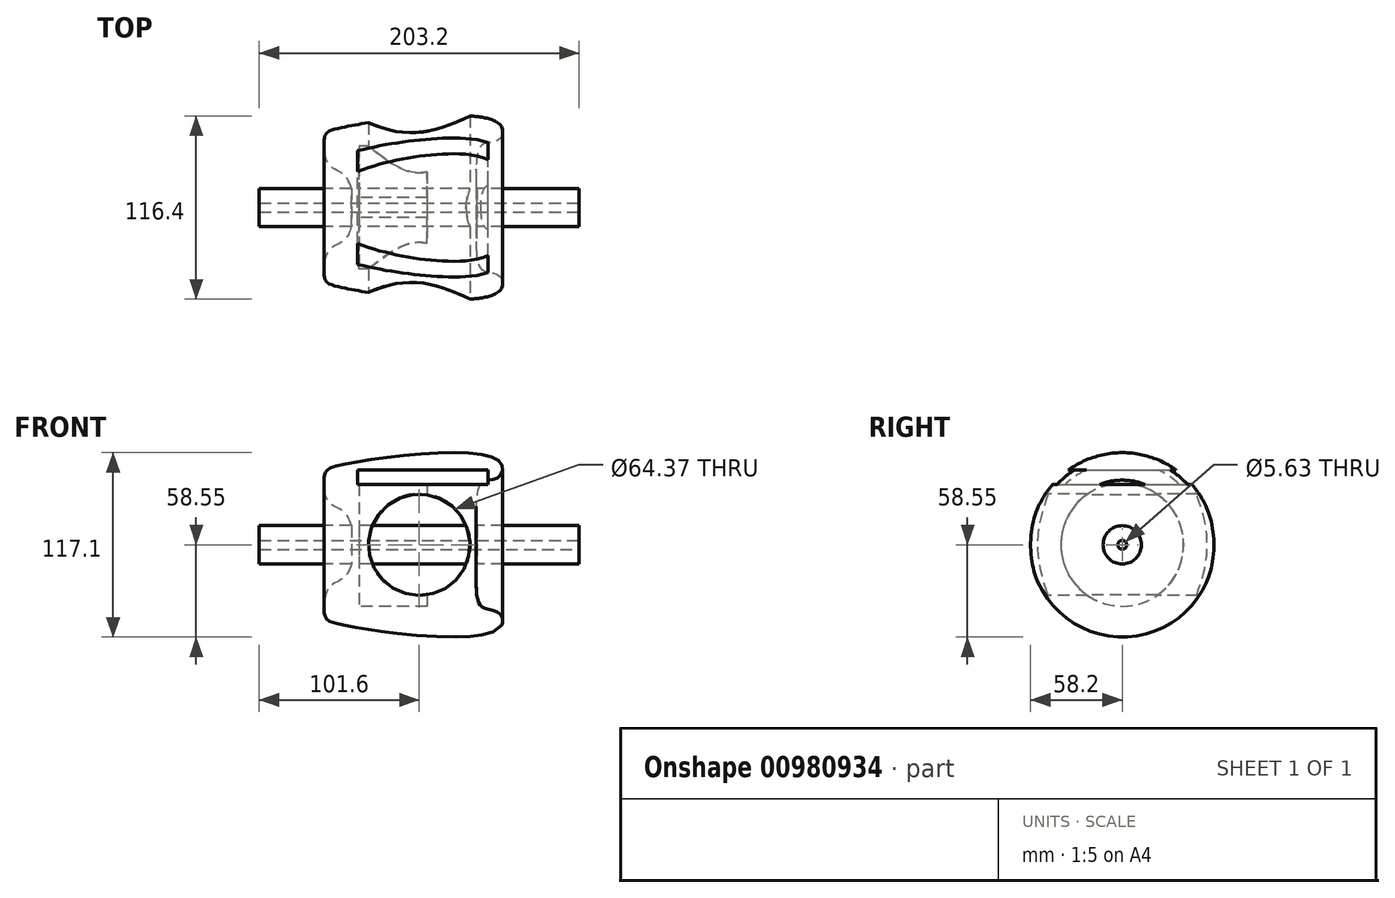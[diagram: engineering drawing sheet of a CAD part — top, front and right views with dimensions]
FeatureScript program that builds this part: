
annotation { "Feature Type Name" : "Feature", "Feature Type Description" : "" }
export const myFeature = defineFeature(function(context is Context, id is Id, definition is map)
    precondition{}
    {
        {
            var Q0;
            Q0=qCreatedBy(makeId("Front.planeOp"),FACE);
            var sketch = newSketch(context, id + "F0", { "sketchPlane" : qUnion([Q0])});
            skFitSpline(sketch, "E0", {"points": [v(-40.54, 0) * mm, v(-47.36, 20.34) * mm, v(-57.74, 27.7) * mm, v(-60.2, 44.09) * mm, v(-52.28, 50.1) * mm, v(49.82, 53.92) * mm, v(50.37, 43) * mm, v(39.45, 39.17) * mm, v(36.44, 15.42) * mm, v(37, 0) * mm], "startDerivative": vector(-37.15, 216.85) * mm, "endDerivative": vector(3.87, -138.09) * mm});
            skLineSegment(sketch, "E1", {"start": v(-86.95, 0) * mm, "end": v(97.05, 0) * mm, "construction": true});
            skLineSegment(sketch, "E2", {"start": v(-40.54, 0) * mm, "end": v(-38.13, 0) * mm});
            skLineSegment(sketch, "E3", {"start": v(-38.13, 0) * mm, "end": v(-38.13, 39) * mm});
            skLineSegment(sketch, "E4", {"start": v(-38.13, 39) * mm, "end": v(4.98, 39) * mm});
            skLineSegment(sketch, "E5", {"start": v(4.98, 39) * mm, "end": v(4.98, 0) * mm});
            skLineSegment(sketch, "E6", {"start": v(4.98, 0) * mm, "end": v(37, 0) * mm});
            skSolve(sketch);
        }
        {
            var Q0;
            Q0 = qSketchRegion(id + "F0", true);
            var Q1;
            Q1=sQuery(id+"F0.wireOp",EDGE,"E1");
            revolve(context, id + "F1", {"surfaceOperationType" : NewSurfaceOperationType.NEW, "entities" : qUnion([Q0]), "axis" : qUnion([Q1]), "revolveType" : RevolveType.FULL});
        }
        {
            var Q0;
            Q0=qCreatedBy(makeId("Front.planeOp"),FACE);
            var sketch = newSketch(context, id + "F2", { "sketchPlane" : qUnion([Q0])});
            skCircle(sketch, "E7", {"center": v(0, 0) * mm, "radius": 32.18 * mm});
            skSolve(sketch);
        }
        {
            var Q0;
            Q0 = qSketchRegion(id + "F2", true);
            extrude(context, id + "F3", {"entities" : qUnion([Q0]), "operationType" : NewBodyOperationType.REMOVE, "endBound" : BoundingType.SYMMETRIC, "oppositeDirection" : true, "depth" : 127 * mm, "offsetDistance" : 25.4 * mm});
        }
        {
            var Q0;
            Q0=qCreatedBy(makeId("Right.planeOp"),FACE);
            var sketch = newSketch(context, id + "F4", { "sketchPlane" : qUnion([Q0])});
            skCircle(sketch, "E8", {"center": v(0, 0) * mm, "radius": 12.2 * mm});
            skSolve(sketch);
        }
        {
            var Q0;
            Q0 = qSketchRegion(id + "F4", true);
            extrude(context, id + "F5", {"entities" : qUnion([Q0]), "operationType" : NewBodyOperationType.ADD, "endBound" : BoundingType.SYMMETRIC, "depth" : 203.2 * mm, "offsetDistance" : 25.4 * mm});
        }
        {
            var Q0;
            Q0=makeQuery(id+"F5.opExtrude","CAP_FACE",FACE,{"disambiguationData":[OSD([sQuery(id+"F4.wireOp",EDGE,"E8")])],"isStart":false});
            var sketch = newSketch(context, id + "F6", { "sketchPlane" : qUnion([Q0])});
            skCircle(sketch, "E9", {"center": v(0, 0) * mm, "radius": 2.81 * mm});
            skSolve(sketch);
        }
        {
            var Q0;
            Q0 = qSketchRegion(id + "F6", true);
            extrude(context, id + "F7", {"entities" : qUnion([Q0]), "operationType" : NewBodyOperationType.REMOVE, "endBound" : BoundingType.THROUGH_ALL, "oppositeDirection" : true, "depth" : 25.4 * mm, "offsetDistance" : 25.4 * mm});
        }
        {
            var Q0;
            Q0=qCreatedBy(makeId("Front.planeOp"),FACE);
            var sketch = newSketch(context, id + "F8", { "sketchPlane" : qUnion([Q0])});
            skLineSegment(sketch, "E10.bottom", {"start": v(-39.13, 47.54) * mm, "end": v(43.8, 47.54) * mm});
            skLineSegment(sketch, "E10.top", {"start": v(-39.13, 38.5) * mm, "end": v(43.8, 38.5) * mm});
            skLineSegment(sketch, "E10.left", {"start": v(-39.13, 47.54) * mm, "end": v(-39.13, 38.5) * mm});
            skLineSegment(sketch, "E10.right", {"start": v(43.8, 47.54) * mm, "end": v(43.8, 38.5) * mm});
            skSolve(sketch);
        }
        {
            var Q0;
            Q0 = qSketchRegion(id + "F8", true);
            extrude(context, id + "F9", {"entities" : qUnion([Q0]), "operationType" : NewBodyOperationType.REMOVE, "endBound" : BoundingType.SYMMETRIC, "depth" : 127 * mm, "offsetDistance" : 25.4 * mm});
        }
    });
